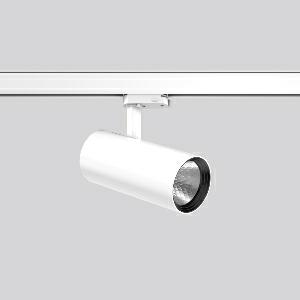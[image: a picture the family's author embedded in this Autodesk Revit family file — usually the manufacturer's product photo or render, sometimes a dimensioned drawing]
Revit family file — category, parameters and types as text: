
# Revit family: deecos_s_mini_742193_002_76_b518
name_source: partatom
category: Lighting Fixtures
units: mm (PartAtom-declared; Revit-internal decimal feet)

## family parameters
Cut with Voids When Loaded = No
Host = Face
Light Source = No
Part Type = Normal
Room Calculation Point = No
Round Connector Dimension = Use Diameter
Shared = No

## types (1)
- DEECOS S mini (1 x LED Modul 930, 2200 lm, 3000)
    Apparent Load = 22 VA
    Approval mark = CE
    CIE Flux Codes = 100 100 100 100 100
    Color Rendering = 90
    Color Temperature = 3000
    Default Elevation = 1800 mm
    Description = Series: DEECOS S mini
LED surface-mounted projector in modern design with no visible cooling ribs. Housing: die-cast aluminium, powder-coated. Rotation range: 356°. Swivel range: 90°. Black plastic ring and recessed LED to prevent glare from the side. Optical assembly with reflector made of MIRO-Silver with 98% total light reflection for outstanding efficiency - can be changed without tools. Best colour rendering index Ra>90. Superspot version with small spot LED. With adapter for RZB 3-circuit DALI tracks. Suitable for Track on ceiling, Wall track. High quality converter without flickering and stroboscopic effect. The following accessories can be mounted without use of tools: interchangeable lenses, decorative glasses, honeycomb louvre, clear and frosted diffusers, white interchangeable plastic ring. 
Colour: traffic white, matt (RAL 9016)
Diameter: 87 mm
Height: 214 mm
Lamp: LED
Socket: without socket
Colour temperature: 3000K
Colour rendering index (CRI): 92
System power: 22 W
Rated luminous flux: 2200 lm
Luminous efficiency: 100 lm/W
Control gear: Converter, dimmable, DALI
Protection class: I
Type of protection: IP 20
    Height = 214 mm
    Lamp = 1 x LED Modul 930
    Lamp Light Flux = 2200 lm
    Lamp count = 1
    Length = 87 mm
    Lifetime = 50000 h
    Luminous efficacy = 100 lm/W
    Manufacturer = RZB
    ModVariant = No
    Model = 742193.002.76
    Mounting Place = Ceiling
    Mounting Type = Rail mounted
    Number of Poles = 1
    OnlyDefault = Yes
    Power Factor = 1
    Product Name = DEECOS S mini
    Product group = Track mounted projectors
    ProductGroupID = 301
    Protection Class = Protection class I
    Protection Degree = IP 20
    RLX_Detail_Level = 1
    RLX_Emergency_Light_Flux = 0 lm
    RLX_Emergency_Type = 0
    RLX_Emergency_Type_DB = No
    RlxData = <blob elided: 35737 chars, md5=79f93340>
    Socket = socket
    Standby Power = 0 W
    System Light Flux = 2200 lm
    System Power = 22 W
    Type Comments = Product without accessories
    Type Image = 741926.002.jpg
    URL = http://relux.com
    VarID = ---
    Voltage = 230 V
    Voltage Range = 220-240 V
    Weight = 0.00 kg
    Width = 0 mm  [stored 0 ft]

note: [stored X ft] marks values corroborated as IEEE doubles in the binary element streams (Revit-internal decimal feet)

## geometry (parser evidence)
native form markers: Blend x4, Sweep x12
no freeform markers — native parametric forms only
